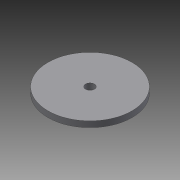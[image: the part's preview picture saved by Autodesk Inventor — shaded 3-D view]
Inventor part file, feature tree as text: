
AUTODESK INVENTOR PART (.ipt)
format: ipt  version: 2015 (Build 190159000, 159)  size: 72,192 bytes
history: native  units: mm
features: extrude x1, sketch x1
ambient origin geometry x8: Origin, YZ Plane, XZ Plane, XY Plane, X Axis, Y Axis, Z Axis, Center Point
bodies: Solid1 (feature_tree)
feature tree (2):
  extrude  "Extrusion1"  Depth=6.0mm
  sketch  "Sketch1"  dims[d0=9.18mm d1=85.75mm d2=6.0mm d3=0.0mm]
